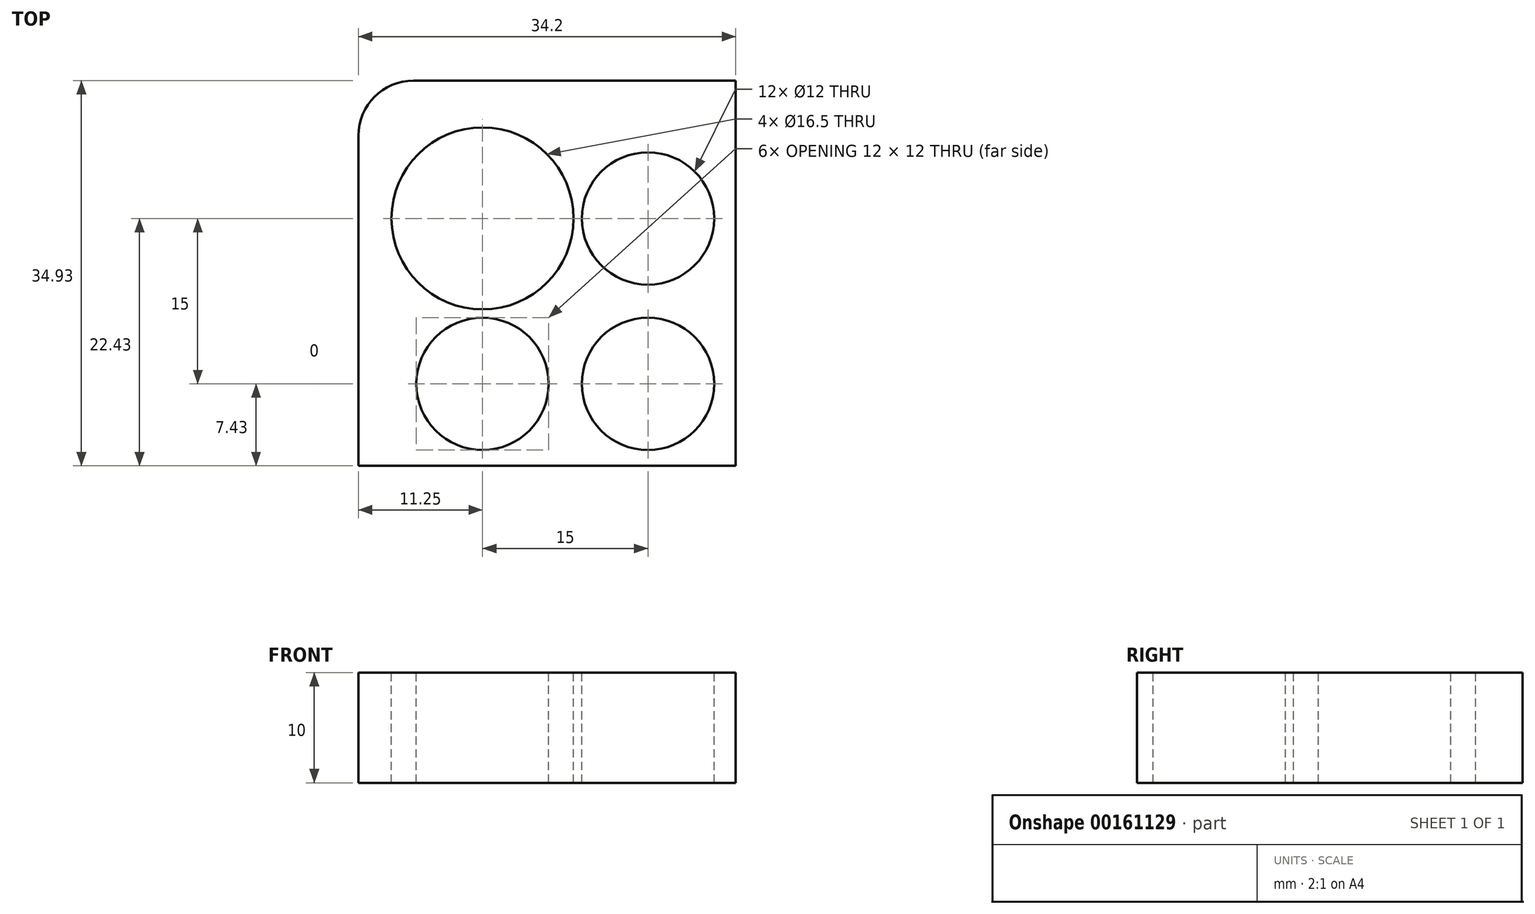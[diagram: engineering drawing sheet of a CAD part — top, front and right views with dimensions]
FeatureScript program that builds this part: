
annotation { "Feature Type Name" : "Feature", "Feature Type Description" : "" }
export const myFeature = defineFeature(function(context is Context, id is Id, definition is map)
    precondition{}
    {
        {
            var Q0;
            Q0=qCreatedBy(makeId("Top.planeOp"),FACE);
            var sketch = newSketch(context, id + "F0", { "sketchPlane" : qUnion([Q0])});
            skLineSegment(sketch, "E0.bottom", {"start": v(58.75, -42.5) * mm, "end": v(-58.75, -42.5) * mm});
            skLineSegment(sketch, "E0.top", {"start": v(58.75, 42.5) * mm, "end": v(-58.75, 42.5) * mm});
            skLineSegment(sketch, "E0.left", {"start": v(63.75, -37.5) * mm, "end": v(63.75, 37.5) * mm});
            skLineSegment(sketch, "E0.right", {"start": v(-63.75, -37.5) * mm, "end": v(-63.75, 37.5) * mm});
            skPoint(sketch, "E0.middle", {"position": v(0, 0) * mm});
            skPoint(sketch, "E1.visualSharp", {"position": v(-63.75, 42.5) * mm});
            skArc(sketch, "E1.filletArc", {"start": v(-58.75, 42.5) * mm, "mid": v(-62.29, 41.04) * mm, "end": v(-63.75, 37.5) * mm});
            skPoint(sketch, "E2.visualSharp", {"position": v(-63.75, -42.5) * mm});
            skArc(sketch, "E2.filletArc", {"start": v(-63.75, -37.5) * mm, "mid": v(-62.29, -41.04) * mm, "end": v(-58.75, -42.5) * mm});
            skPoint(sketch, "E3.visualSharp", {"position": v(63.75, -42.5) * mm});
            skArc(sketch, "E3.filletArc", {"start": v(58.75, -42.5) * mm, "mid": v(62.29, -41.04) * mm, "end": v(63.75, -37.5) * mm});
            skPoint(sketch, "E4.visualSharp", {"position": v(63.75, 42.5) * mm});
            skArc(sketch, "E4.filletArc", {"start": v(63.75, 37.5) * mm, "mid": v(62.29, 41.04) * mm, "end": v(58.75, 42.5) * mm});
            skSolve(sketch);
        }
        {
            var Q0;
            Q0=qSketchRegion(id+"F0",true);
            extrude(context, id + "F1", {"entities" : qUnion([Q0]), "depth" : 25 * mm});
        }
        {
            var Q0;
            Q0=makeQuery(id+"F1.opExtrude","CAP_FACE",FACE,{"disambiguationData":[OSD([sQuery(id+"F0.wireOp",EDGE,"E0.bottom"),sQuery(id+"F0.wireOp",EDGE,"E0.top"),sQuery(id+"F0.wireOp",EDGE,"E0.left"),sQuery(id+"F0.wireOp",EDGE,"E0.right"),sQuery(id+"F0.wireOp",EDGE,"E1.filletArc"),sQuery(id+"F0.wireOp",EDGE,"E2.filletArc"),sQuery(id+"F0.wireOp",EDGE,"E3.filletArc"),sQuery(id+"F0.wireOp",EDGE,"E4.filletArc")])],"isStart":false});
            var sketch = newSketch(context, id + "F2", { "sketchPlane" : qUnion([Q0])});
            skCircle(sketch, "E5.0.1.0", {"center": v(-52.5, 15) * mm, "radius": 6 * mm});
            skCircle(sketch, "E5.0.2.0", {"center": v(-52.5, 0) * mm, "radius": 6 * mm});
            skCircle(sketch, "E5.0.3.0", {"center": v(-52.5, -15) * mm, "radius": 6 * mm});
            skCircle(sketch, "E5.1.0.0", {"center": v(-37.5, 30) * mm, "radius": 6 * mm});
            skCircle(sketch, "E5.1.1.0", {"center": v(-37.5, 15) * mm, "radius": 6 * mm});
            skCircle(sketch, "E5.1.2.0", {"center": v(-37.5, 0) * mm, "radius": 6 * mm});
            skCircle(sketch, "E5.1.3.0", {"center": v(-37.5, -15) * mm, "radius": 6 * mm});
            skCircle(sketch, "E5.1.4.0", {"center": v(-37.5, -30) * mm, "radius": 6 * mm});
            skCircle(sketch, "E5.2.0.0", {"center": v(-22.5, 30) * mm, "radius": 6 * mm});
            skCircle(sketch, "E5.2.1.0", {"center": v(-22.5, 15) * mm, "radius": 6 * mm});
            skCircle(sketch, "E5.2.2.0", {"center": v(-22.5, 0) * mm, "radius": 6 * mm});
            skCircle(sketch, "E5.2.3.0", {"center": v(-22.5, -15) * mm, "radius": 6 * mm});
            skCircle(sketch, "E5.2.4.0", {"center": v(-22.5, -30) * mm, "radius": 6 * mm});
            skCircle(sketch, "E5.3.0.0", {"center": v(-7.5, 30) * mm, "radius": 6 * mm});
            skCircle(sketch, "E5.3.1.0", {"center": v(-7.5, 15) * mm, "radius": 6 * mm});
            skCircle(sketch, "E5.3.2.0", {"center": v(-7.5, 0) * mm, "radius": 6 * mm});
            skCircle(sketch, "E5.3.3.0", {"center": v(-7.5, -15) * mm, "radius": 6 * mm});
            skCircle(sketch, "E5.3.4.0", {"center": v(-7.5, -30) * mm, "radius": 6 * mm});
            skCircle(sketch, "E5.4.0.0", {"center": v(7.5, 30) * mm, "radius": 6 * mm});
            skCircle(sketch, "E5.4.1.0", {"center": v(7.5, 15) * mm, "radius": 6 * mm});
            skCircle(sketch, "E5.4.2.0", {"center": v(7.5, 0) * mm, "radius": 6 * mm});
            skCircle(sketch, "E5.4.3.0", {"center": v(7.5, -15) * mm, "radius": 6 * mm});
            skCircle(sketch, "E5.4.4.0", {"center": v(7.5, -30) * mm, "radius": 6 * mm});
            skCircle(sketch, "E5.5.0.0", {"center": v(22.5, 30) * mm, "radius": 6 * mm});
            skCircle(sketch, "E5.5.1.0", {"center": v(22.5, 15) * mm, "radius": 6 * mm});
            skCircle(sketch, "E5.5.2.0", {"center": v(22.5, 0) * mm, "radius": 6 * mm});
            skCircle(sketch, "E5.5.3.0", {"center": v(22.5, -15) * mm, "radius": 6 * mm});
            skCircle(sketch, "E5.5.4.0", {"center": v(22.5, -30) * mm, "radius": 6 * mm});
            skCircle(sketch, "E5.6.0.0", {"center": v(37.5, 30) * mm, "radius": 6 * mm});
            skCircle(sketch, "E5.6.1.0", {"center": v(37.5, 15) * mm, "radius": 6 * mm});
            skCircle(sketch, "E5.6.2.0", {"center": v(37.5, 0) * mm, "radius": 6 * mm});
            skCircle(sketch, "E5.6.3.0", {"center": v(37.5, -15) * mm, "radius": 6 * mm});
            skCircle(sketch, "E5.6.4.0", {"center": v(37.5, -30) * mm, "radius": 6 * mm});
            skCircle(sketch, "E5.7.1.0", {"center": v(52.5, 15) * mm, "radius": 6 * mm});
            skCircle(sketch, "E5.7.2.0", {"center": v(52.5, 0) * mm, "radius": 6 * mm});
            skCircle(sketch, "E5.7.3.0", {"center": v(52.5, -15) * mm, "radius": 6 * mm});
            skLineSegment(sketch, "E5.direction1", {"start": v(-52.5, 30) * mm, "end": v(-37.5, 30) * mm, "construction": true});
            skLineSegment(sketch, "E5.direction2", {"start": v(-52.5, 30) * mm, "end": v(-52.5, 15) * mm, "construction": true});
            skCircle(sketch, "E6", {"center": v(-52.5, 30) * mm, "radius": 8.25 * mm});
            skCircle(sketch, "E7", {"center": v(-52.5, -30) * mm, "radius": 8 * mm});
            skCircle(sketch, "E8", {"center": v(52.5, 30) * mm, "radius": 8 * mm});
            skCircle(sketch, "E9", {"center": v(52.5, -30) * mm, "radius": 8 * mm});
            skSolve(sketch);
        }
        {
            var Q0;
            Q0=qSketchRegion(id+"F2",true);
            extrude(context, id + "F3", {"entities" : qUnion([Q0]), "operationType" : NewBodyOperationType.REMOVE, "oppositeDirection" : true, "depth" : 20 * mm});
        }
        {
            var Q0;
            Q0=makeQuery(id+"F1.opExtrude","CAP_FACE",FACE,{"disambiguationData":[OSD([sQuery(id+"F0.wireOp",EDGE,"E0.bottom"),sQuery(id+"F0.wireOp",EDGE,"E0.top"),sQuery(id+"F0.wireOp",EDGE,"E0.left"),sQuery(id+"F0.wireOp",EDGE,"E0.right"),sQuery(id+"F0.wireOp",EDGE,"E1.filletArc"),sQuery(id+"F0.wireOp",EDGE,"E2.filletArc"),sQuery(id+"F0.wireOp",EDGE,"E3.filletArc"),sQuery(id+"F0.wireOp",EDGE,"E4.filletArc")])],"isStart":false});
            var sketch = newSketch(context, id + "F4", { "sketchPlane" : qUnion([Q0])});
            skLineSegment(sketch, "E10", {"start": v(69.58, 48.73) * mm, "end": v(69.58, -59.45) * mm});
            skLineSegment(sketch, "E11", {"start": v(69.58, -59.45) * mm, "end": v(-74.26, -59.45) * mm});
            skLineSegment(sketch, "E12", {"start": v(-74.26, -59.45) * mm, "end": v(-74.26, 4.95) * mm});
            skLineSegment(sketch, "E13", {"start": v(-74.26, 4.95) * mm, "end": v(-74.26, 7.57) * mm});
            skLineSegment(sketch, "E14", {"start": v(-74.26, 7.57) * mm, "end": v(-29.55, 7.57) * mm});
            skLineSegment(sketch, "E15", {"start": v(-29.55, 7.57) * mm, "end": v(-29.55, 48.73) * mm});
            skLineSegment(sketch, "E16", {"start": v(-29.55, 48.73) * mm, "end": v(69.58, 48.73) * mm});
            skSolve(sketch);
        }
        {
            var Q0;
            Q0 = qSketchRegion(id + "F4", true);
            extrude(context, id + "F5", {"entities" : qUnion([Q0]), "operationType" : NewBodyOperationType.REMOVE, "endBound" : BoundingType.THROUGH_ALL, "oppositeDirection" : true, "depth" : 25 * mm});
        }
        {
            var Q0;
            Q0=makeQuery(id+"F5.boolean.opBoolean","COPY",FACE,{"derivedFrom":makeQuery(id+"F5.opExtrude","SWEPT_FACE",FACE,{"disambiguationData":[OSD([sQuery(id+"F4.wireOp",EDGE,"E15")])]})});
            var sketch = newSketch(context, id + "F6", { "sketchPlane" : qUnion([Q0])});
            skLineSegment(sketch, "E17.bottom", {"start": v(7.57, 0) * mm, "end": v(42.5, 0) * mm});
            skLineSegment(sketch, "E17.top", {"start": v(7.57, 15) * mm, "end": v(42.5, 15) * mm});
            skLineSegment(sketch, "E17.left", {"start": v(7.57, 0) * mm, "end": v(7.57, 15) * mm});
            skLineSegment(sketch, "E17.right", {"start": v(42.5, 0) * mm, "end": v(42.5, 15) * mm});
            skSolve(sketch);
        }
        {
            var Q0;
            Q0 = qSketchRegion(id + "F6", true);
            extrude(context, id + "F7", {"entities" : qUnion([Q0]), "operationType" : NewBodyOperationType.REMOVE, "endBound" : BoundingType.THROUGH_ALL, "oppositeDirection" : true, "depth" : 25 * mm});
        }
    });
